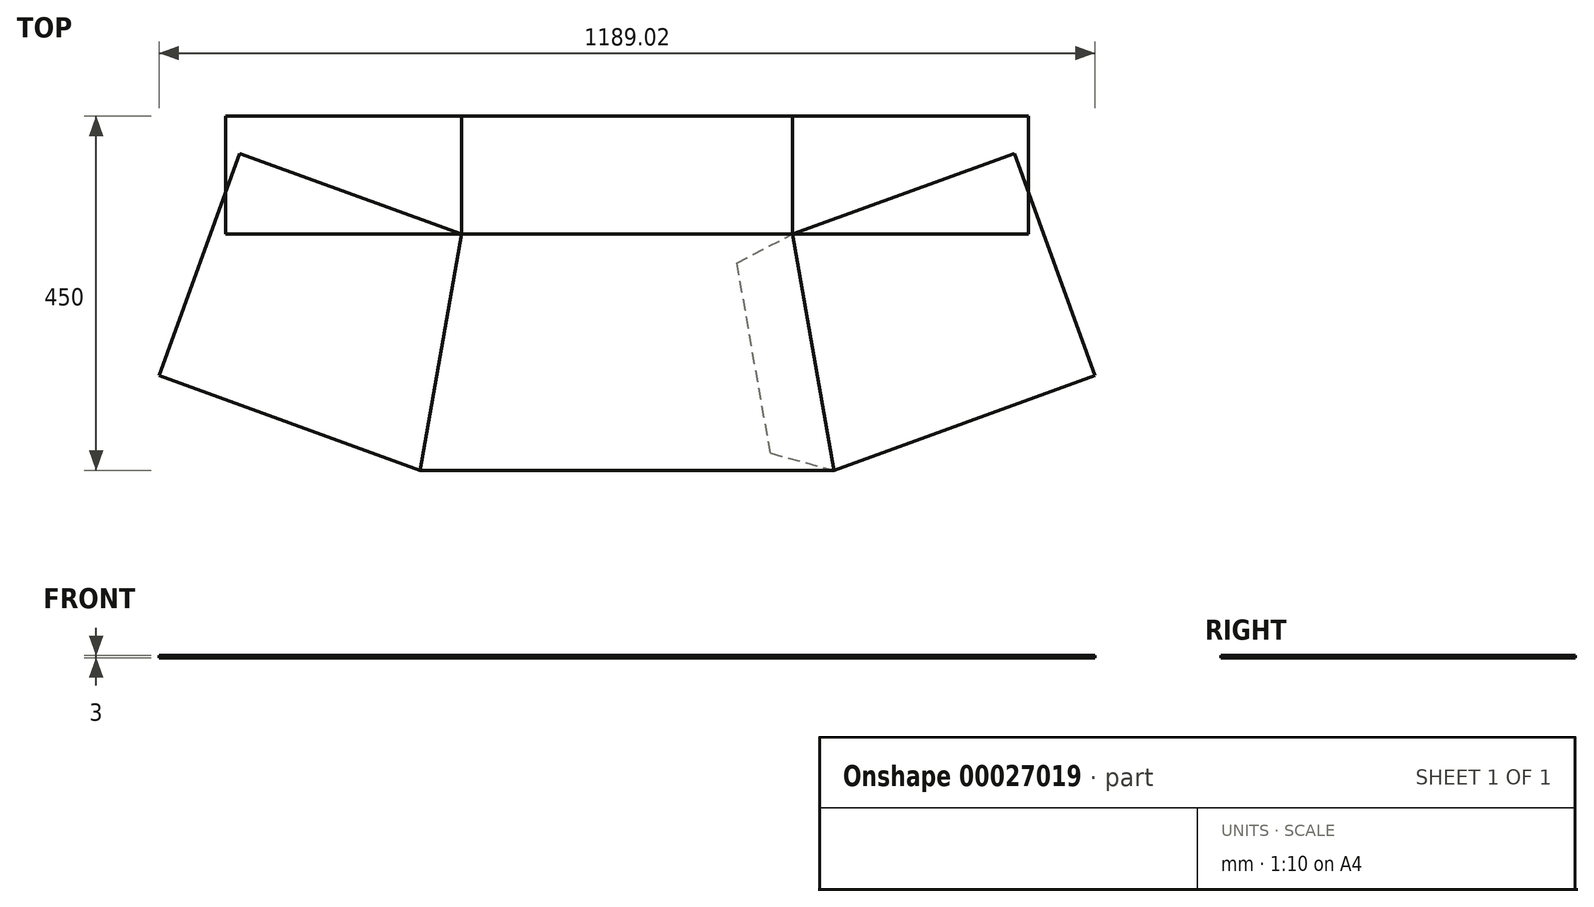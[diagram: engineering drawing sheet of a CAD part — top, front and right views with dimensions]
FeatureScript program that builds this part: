
annotation { "Feature Type Name" : "Feature", "Feature Type Description" : "" }
export const myFeature = defineFeature(function(context is Context, id is Id, definition is map)
    precondition{}
    {
        {
            var Q0;
            Q0=qCreatedBy(makeId("Top.planeOp"),FACE);
            var sketch = newSketch(context, id + "F0", { "sketchPlane" : qUnion([Q0])});
            skLineSegment(sketch, "E0.rect.bottom", {"start": v(-210, 27.07) * mm, "end": v(0, 27.07) * mm});
            skLineSegment(sketch, "E0.rect.top", {"start": v(-262.9, -272.93) * mm, "end": v(0, -272.93) * mm});
            skLineSegment(sketch, "E1.top", {"start": v(-210, 177.07) * mm, "end": v(0, 177.07) * mm});
            skLineSegment(sketch, "E1.left", {"start": v(-210, 27.07) * mm, "end": v(-210, 177.07) * mm});
            skLineSegment(sketch, "E2.bottom", {"start": v(-262.9, -272.93) * mm, "end": v(-262.9, -272.93) * mm});
            skLineSegment(sketch, "E3", {"start": v(-262.9, -272.93) * mm, "end": v(-210, 27.07) * mm});
            skLineSegment(sketch, "E4", {"start": v(0, 8.58) * mm, "end": v(0, -498.58) * mm, "construction": true});
            skLineSegment(sketch, "E5.MirrorCS", {"start": v(-210, 27.07) * mm, "end": v(-510, 27.07) * mm});
            skLineSegment(sketch, "E6.MirrorCS", {"start": v(-510, 27.07) * mm, "end": v(-510, 177.07) * mm});
            skLineSegment(sketch, "E7.MirrorCS", {"start": v(-491.9, 129.68) * mm, "end": v(-594.51, -152.23) * mm});
            skLineSegment(sketch, "E8.MirrorCS", {"start": v(-262.9, -272.93) * mm, "end": v(-594.51, -152.23) * mm});
            skLineSegment(sketch, "E9", {"start": v(-510, 177.07) * mm, "end": v(-210, 177.07) * mm});
            skLineSegment(sketch, "E10", {"start": v(-210, 27.07) * mm, "end": v(-491.9, 129.68) * mm});
            skLineSegment(sketch, "E11.MirrorCS", {"start": v(210, 27.07) * mm, "end": v(0, 27.07) * mm});
            skLineSegment(sketch, "E12.MirrorCS", {"start": v(262.9, -272.93) * mm, "end": v(594.51, -152.23) * mm});
            skLineSegment(sketch, "E13.MirrorCS", {"start": v(210, 27.07) * mm, "end": v(491.9, 129.68) * mm});
            skLineSegment(sketch, "E14.MirrorCS", {"start": v(210, 27.07) * mm, "end": v(510, 27.07) * mm});
            skLineSegment(sketch, "E15.MirrorCS", {"start": v(262.9, -272.93) * mm, "end": v(0, -272.93) * mm});
            skLineSegment(sketch, "E16.MirrorCS", {"start": v(210, 177.07) * mm, "end": v(0, 177.07) * mm});
            skLineSegment(sketch, "E17.MirrorCS", {"start": v(510, 27.07) * mm, "end": v(510, 177.07) * mm});
            skLineSegment(sketch, "E18.MirrorCS", {"start": v(491.9, 129.68) * mm, "end": v(594.51, -152.23) * mm});
            skLineSegment(sketch, "E19.MirrorCS", {"start": v(262.9, -272.93) * mm, "end": v(210, 27.07) * mm});
            skLineSegment(sketch, "E20.MirrorCS", {"start": v(210, 27.07) * mm, "end": v(210, 177.07) * mm});
            skLineSegment(sketch, "E21.MirrorCS", {"start": v(510, 177.07) * mm, "end": v(210, 177.07) * mm});
            skLineSegment(sketch, "E22.MirrorCS", {"start": v(262.9, -272.93) * mm, "end": v(262.9, -272.93) * mm});
            skSolve(sketch);
        }
        {
            var Q0;
            Q0=makeQuery(id+"F0.imprint","IMPRINT",FACE,{"disambiguationData":[TD([[makeQuery(id+"F0.imprint","IMPRINT",EDGE,{"derivedFrom":sQuery(id+"F0.wireOp",EDGE,"E0.rect.top")}),1.0]])]});
            extrude(context, id + "F1", {"entities" : qUnion([Q0]), "depth" : 3 * mm});
        }
        {
            var Q0;
            Q0=makeQuery(id+"F0.imprint","IMPRINT",FACE,{"disambiguationData":[TD([[makeQuery(id+"F0.imprint","IMPRINT",EDGE,{"derivedFrom":sQuery(id+"F0.wireOp",EDGE,"E3")}),1.0]])]});
            var Q1;
            {var subQ4=sQuery(id+"F0.wireOp",EDGE,"E5.MirrorCS");Q1=makeQuery(id+"F0.imprint","IMPRINT",FACE,{"disambiguationData":[TD([[makeQuery(id+"F0.imprint","IMPRINT",EDGE,{"derivedFrom":subQ4}),-1.0]])]});}
            extrude(context, id + "F2", {"entities" : qUnion([Q0, Q1]), "depth" : 3 * mm});
        }
        {
            var Q0;
            {var subQ3=sQuery(id+"F0.wireOp",EDGE,"E12.MirrorCS");Q0=makeQuery(id+"F0.imprint","IMPRINT",FACE,{"disambiguationData":[TD([[makeQuery(id+"F0.imprint","IMPRINT",EDGE,{"derivedFrom":subQ3}),1.0]])]});}
            var Q1;
            {var subQ3=sQuery(id+"F0.wireOp",EDGE,"E13.MirrorCS");Q1=makeQuery(id+"F0.imprint","IMPRINT",FACE,{"disambiguationData":[TD([[makeQuery(id+"F0.imprint","IMPRINT",EDGE,{"derivedFrom":subQ3}),-1.0]])]});}
            extrude(context, id + "F3", {"entities" : qUnion([Q0, Q1]), "depth" : 3 * mm});
        }
        {
            var Q0;
            Q0=makeQuery(id+"F0.imprint","IMPRINT",FACE,{"disambiguationData":[TD([[makeQuery(id+"F0.imprint","IMPRINT",EDGE,{"derivedFrom":sQuery(id+"F0.wireOp",EDGE,"E1.left")}),1.0]])]});
            var Q1;
            {var subQ4=sQuery(id+"F0.wireOp",EDGE,"E5.MirrorCS");Q1=makeQuery(id+"F0.imprint","IMPRINT",FACE,{"disambiguationData":[TD([[makeQuery(id+"F0.imprint","IMPRINT",EDGE,{"derivedFrom":subQ4}),-1.0]])]});}
            extrude(context, id + "F4", {"entities" : qUnion([Q0, Q1]), "depth" : 3 * mm});
        }
        {
            var Q0;
            Q0=makeQuery(id+"F0.imprint","IMPRINT",FACE,{"disambiguationData":[TD([[makeQuery(id+"F0.imprint","IMPRINT",EDGE,{"derivedFrom":sQuery(id+"F0.wireOp",EDGE,"E0.rect.bottom")}),1.0]])]});
            extrude(context, id + "F5", {"entities" : qUnion([Q0]), "depth" : 3 * mm});
        }
        {
            var Q0;
            {var subQ4=sQuery(id+"F0.wireOp",EDGE,"E13.MirrorCS");Q0=makeQuery(id+"F0.imprint","IMPRINT",FACE,{"disambiguationData":[TD([[makeQuery(id+"F0.imprint","IMPRINT",EDGE,{"derivedFrom":subQ4}),1.0]])]});}
            var Q1;
            {var subQ3=sQuery(id+"F0.wireOp",EDGE,"E13.MirrorCS");Q1=makeQuery(id+"F0.imprint","IMPRINT",FACE,{"disambiguationData":[TD([[makeQuery(id+"F0.imprint","IMPRINT",EDGE,{"derivedFrom":subQ3}),-1.0]])]});}
            extrude(context, id + "F6", {"entities" : qUnion([Q0, Q1]), "depth" : 3 * mm});
        }
        {
            var Q0;
            Q0=qCreatedBy(makeId("Top.planeOp"),FACE);
            var sketch = newSketch(context, id + "F7", { "sketchPlane" : qUnion([Q0])});
            skLineSegment(sketch, "E23", {"start": v(182.16, -251.09) * mm, "end": v(139.52, -9.28) * mm});
            skLineSegment(sketch, "E24.0", {"start": v(262.9, -272.93) * mm, "end": v(210, 27.07) * mm});
            skLineSegment(sketch, "E25", {"start": v(182.16, -251.09) * mm, "end": v(262.9, -272.93) * mm});
            skLineSegment(sketch, "E26", {"start": v(139.52, -9.28) * mm, "end": v(210, 27.07) * mm});
            skSolve(sketch);
        }
        {
            var Q0;
            Q0=makeQuery(id+"F7.imprint","IMPRINT",FACE,{"disambiguationData":[TD([[makeQuery(id+"F7.imprint","IMPRINT",EDGE,{"derivedFrom":sQuery(id+"F7.wireOp",EDGE,"E23")}),-1.0]])]});
            extrude(context, id + "F8", {"entities" : qUnion([Q0]), "depth" : 1 * mm});
        }
    });
